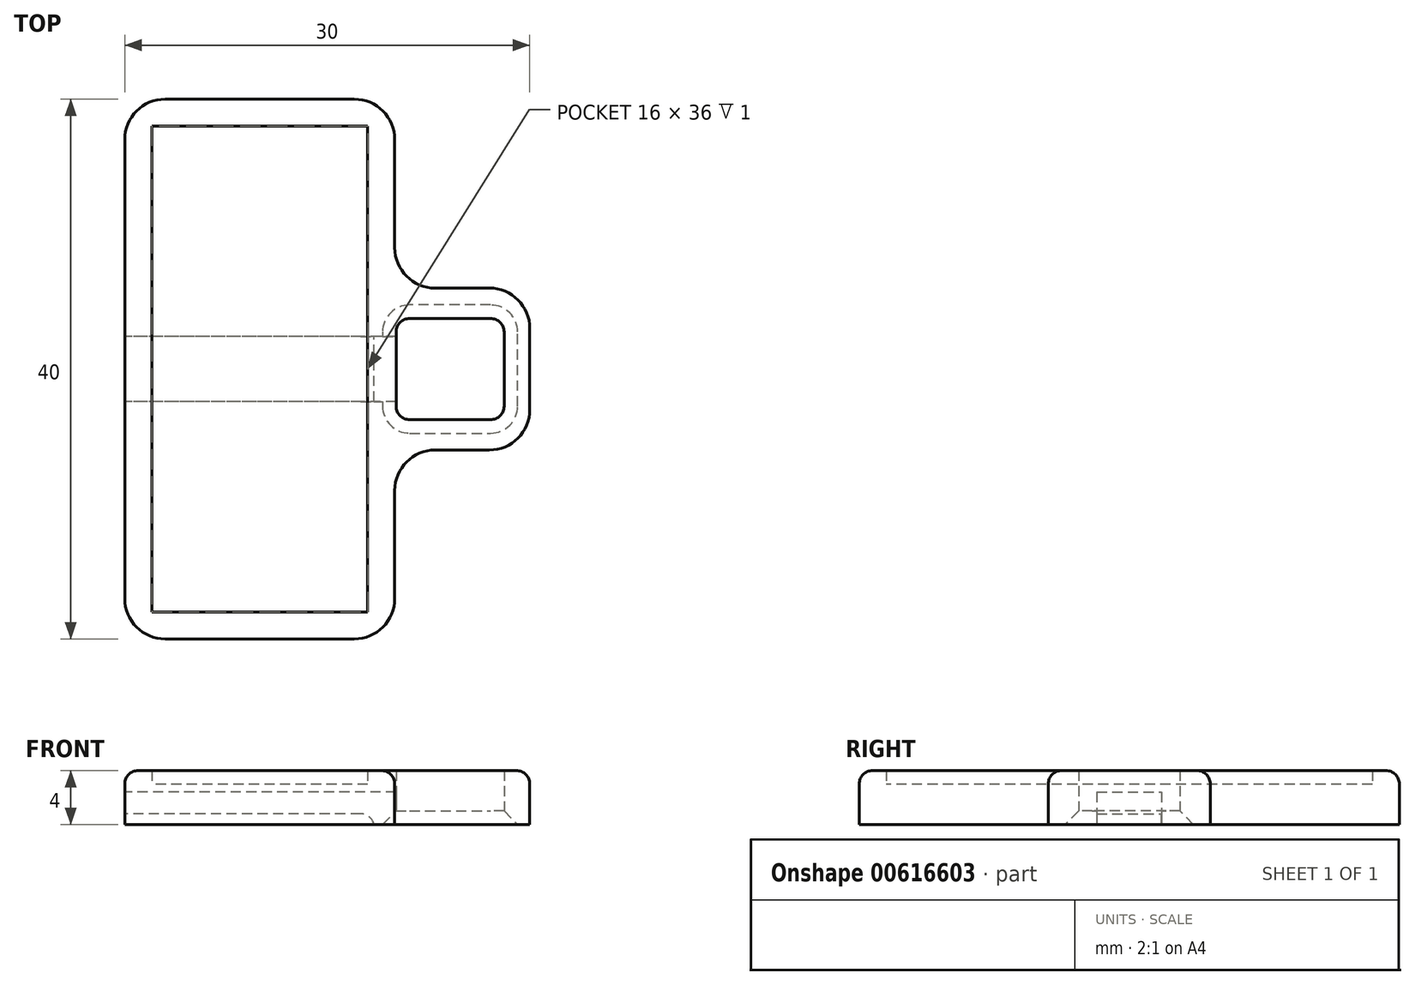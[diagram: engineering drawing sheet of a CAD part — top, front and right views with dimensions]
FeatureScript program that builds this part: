
annotation { "Feature Type Name" : "Feature", "Feature Type Description" : "" }
export const myFeature = defineFeature(function(context is Context, id is Id, definition is map)
    precondition{}
    {
        {
            var Q0;
            Q0=qCreatedBy(makeId("Top.planeOp"),FACE);
            var sketch = newSketch(context, id + "F0", { "sketchPlane" : qUnion([Q0])});
            skLineSegment(sketch, "E0.bottom", {"start": v(7, 20) * mm, "end": v(-7, 20) * mm});
            skLineSegment(sketch, "E0.top", {"start": v(7, -20) * mm, "end": v(-7, -20) * mm});
            skLineSegment(sketch, "E0.left", {"start": v(10, -9) * mm, "end": v(10, -17) * mm});
            skLineSegment(sketch, "E0.right", {"start": v(-10, 17) * mm, "end": v(-10, -17) * mm});
            skPoint(sketch, "E0.middle", {"position": v(0, 0) * mm});
            skLineSegment(sketch, "E1.bottom", {"start": v(13, 6) * mm, "end": v(17, 6) * mm});
            skLineSegment(sketch, "E1.top", {"start": v(13, -6) * mm, "end": v(17, -6) * mm});
            skLineSegment(sketch, "E1.right", {"start": v(20, 3) * mm, "end": v(20, -3) * mm});
            skPoint(sketch, "E1.middle", {"position": v(14.1, 0) * mm});
            skLineSegment(sketch, "E2.0", {"start": v(8, 18) * mm, "end": v(-8, 18) * mm});
            skLineSegment(sketch, "E2.1", {"start": v(8, 18) * mm, "end": v(8, -18) * mm});
            skLineSegment(sketch, "E2.2", {"start": v(8, -18) * mm, "end": v(-8, -18) * mm});
            skLineSegment(sketch, "E2.3", {"start": v(-8, 18) * mm, "end": v(-8, -18) * mm});
            skPoint(sketch, "E3.visualSharp", {"position": v(-10, 20) * mm});
            skArc(sketch, "E3.filletArc", {"start": v(-7, 20) * mm, "mid": v(-9.12, 19.12) * mm, "end": v(-10, 17) * mm});
            skPoint(sketch, "E4.visualSharp", {"position": v(10, 20) * mm});
            skArc(sketch, "E4.filletArc", {"start": v(10, 17) * mm, "mid": v(9.12, 19.12) * mm, "end": v(7, 20) * mm});
            skPoint(sketch, "E5.visualSharp", {"position": v(10, -20) * mm});
            skArc(sketch, "E5.filletArc", {"start": v(7, -20) * mm, "mid": v(9.12, -19.12) * mm, "end": v(10, -17) * mm});
            skPoint(sketch, "E6.visualSharp", {"position": v(-10, -20) * mm});
            skArc(sketch, "E6.filletArc", {"start": v(-10, -17) * mm, "mid": v(-9.12, -19.12) * mm, "end": v(-7, -20) * mm});
            skPoint(sketch, "E7.visualSharp", {"position": v(20, 6) * mm});
            skArc(sketch, "E7.filletArc", {"start": v(20, 3) * mm, "mid": v(19.12, 5.12) * mm, "end": v(17, 6) * mm});
            skPoint(sketch, "E8.visualSharp", {"position": v(20, -6) * mm});
            skArc(sketch, "E8.filletArc", {"start": v(17, -6) * mm, "mid": v(19.12, -5.12) * mm, "end": v(20, -3) * mm});
            skPoint(sketch, "E9.newPointA", {"position": v(12, -6) * mm});
            skArc(sketch, "E9.filletArc", {"start": v(13, -6) * mm, "mid": v(10.88, -6.88) * mm, "end": v(10, -9) * mm});
            skLineSegment(sketch, "E10", {"start": v(10, 17) * mm, "end": v(10, 9) * mm});
            skPoint(sketch, "E11.visualSharp", {"position": v(10, 6) * mm});
            skArc(sketch, "E11.filletArc", {"start": v(10, 9) * mm, "mid": v(10.88, 6.88) * mm, "end": v(13, 6) * mm});
            skLineSegment(sketch, "E12.bottom", {"start": v(11.1, 3.75) * mm, "end": v(17.1, 3.75) * mm});
            skLineSegment(sketch, "E12.top", {"start": v(11.1, -3.75) * mm, "end": v(17.1, -3.75) * mm});
            skLineSegment(sketch, "E12.left", {"start": v(10.1, 2.75) * mm, "end": v(10.1, -2.75) * mm});
            skLineSegment(sketch, "E12.right", {"start": v(18.1, 2.75) * mm, "end": v(18.1, -2.75) * mm});
            skPoint(sketch, "E13.visualSharp", {"position": v(10.1, 3.75) * mm});
            skArc(sketch, "E13.filletArc", {"start": v(11.1, 3.75) * mm, "mid": v(10.4, 3.46) * mm, "end": v(10.1, 2.75) * mm});
            skPoint(sketch, "E14.visualSharp", {"position": v(10.1, -3.75) * mm});
            skArc(sketch, "E14.filletArc", {"start": v(10.1, -2.75) * mm, "mid": v(10.4, -3.46) * mm, "end": v(11.1, -3.75) * mm});
            skPoint(sketch, "E15.visualSharp", {"position": v(18.1, -3.75) * mm});
            skArc(sketch, "E15.filletArc", {"start": v(17.1, -3.75) * mm, "mid": v(17.8, -3.46) * mm, "end": v(18.1, -2.75) * mm});
            skPoint(sketch, "E16.visualSharp", {"position": v(18.1, 3.75) * mm});
            skArc(sketch, "E16.filletArc", {"start": v(18.1, 2.75) * mm, "mid": v(17.8, 3.46) * mm, "end": v(17.1, 3.75) * mm});
            skSolve(sketch);
        }
        {
            var Q0;
            Q0=makeQuery(id+"F0.imprint","IMPRINT",FACE,{"disambiguationData":[TD([[makeQuery(id+"F0.imprint","IMPRINT",EDGE,{"derivedFrom":sQuery(id+"F0.wireOp",EDGE,"E0.bottom")}),1.0]])]});
            extrude(context, id + "F1", {"entities" : qUnion([Q0]), "depth" : 4 * mm, "offsetDistance" : 25 * mm});
        }
        {
            var Q0;
            Q0=makeQuery(id+"F0.imprint","IMPRINT",FACE,{"disambiguationData":[TD([[makeQuery(id+"F0.imprint","IMPRINT",EDGE,{"derivedFrom":sQuery(id+"F0.wireOp",EDGE,"E2.0")}),1.0]])]});
            extrude(context, id + "F2", {"entities" : qUnion([Q0]), "operationType" : NewBodyOperationType.ADD, "depth" : 3 * mm, "offsetDistance" : 25 * mm});
        }
        {
            var Q0;
            Q0=makeQuery(id+"F1.opExtrude","SWEPT_FACE",FACE,{"disambiguationData":[OSD([sQuery(id+"F0.wireOp",EDGE,"E0.right")])]});
            var sketch = newSketch(context, id + "F3", { "sketchPlane" : qUnion([Q0])});
            skLineSegment(sketch, "E17.bottom", {"start": v(2.4, 2.4) * mm, "end": v(-2.4, 2.4) * mm});
            skLineSegment(sketch, "E17.top", {"start": v(2.4, 0.8) * mm, "end": v(-2.4, 0.8) * mm});
            skLineSegment(sketch, "E17.left", {"start": v(2.4, 2.4) * mm, "end": v(2.4, 0.8) * mm});
            skLineSegment(sketch, "E17.right", {"start": v(-2.4, 2.4) * mm, "end": v(-2.4, 0.8) * mm});
            skPoint(sketch, "E17.middle", {"position": v(0, 1.6) * mm});
            skSolve(sketch);
        }
        {
            var Q0;
            Q0=makeQuery(id+"F3.imprint","IMPRINT",FACE,{"disambiguationData":[TD([[makeQuery(id+"F3.imprint","IMPRINT",EDGE,{"derivedFrom":sQuery(id+"F3.wireOp",EDGE,"E17.bottom")}),1.0]])]});
            var Q1;
            Q1=makeQuery(id+"F1.opExtrude","SWEPT_FACE",FACE,{"disambiguationData":[OSD([sQuery(id+"F0.wireOp",EDGE,"E12.left")])]});
            extrude(context, id + "F4", {"entities" : qUnion([Q0]), "operationType" : NewBodyOperationType.REMOVE, "endBound" : BoundingType.UP_TO_SURFACE, "oppositeDirection" : true, "depth" : 25 * mm, "endBoundEntityFace" : qUnion([Q1]), "offsetDistance" : 25 * mm});
        }
        {
            var Q0;
            Q0=makeQuery(id+"F1.opExtrude","CAP_EDGE",EDGE,{"disambiguationData":[OSD([sQuery(id+"F0.wireOp",EDGE,"E12.right")])],"isStart":true});
            chamfer(context, id + "F5", {"entities" : qUnion([Q0]), "width" : 1 * mm, "tangentPropagation" : true});
        }
        {
            var Q0;
            Q0=makeQuery(id+"F5.opChamfer","BLEND_EDGE",EDGE,{"blendedFrom":[makeQuery(id+"F1.opExtrude","CAP_EDGE",EDGE,{"disambiguationData":[OSD([sQuery(id+"F0.wireOp",EDGE,"E12.left")])],"isStart":true}),makeQuery(id+"F4.boolean.opBoolean","COPY",FACE,{"derivedFrom":makeQuery(id+"F4.opExtrude","SWEPT_FACE",FACE,{"disambiguationData":[OSD([sQuery(id+"F3.wireOp",EDGE,"E17.top")])]})})],"blendedInto":[makeQuery(id+"F4.boolean.opBoolean","COPY",FACE,{"derivedFrom":makeQuery(id+"F4.opExtrude","SWEPT_FACE",FACE,{"disambiguationData":[OSD([sQuery(id+"F3.wireOp",EDGE,"E17.top")])]})})]});
            fillet(context, id + "F6", {"entities" : qUnion([Q0]), "radius" : 1 * mm, "tangentPropagation" : true, "allowEdgeOverflow" : false});
        }
        {
            var Q0;
            Q0=makeQuery(id+"F1.opExtrude","CAP_EDGE",EDGE,{"disambiguationData":[OSD([sQuery(id+"F0.wireOp",EDGE,"E0.right")])],"isStart":false});
            fillet(context, id + "F7", {"entities" : qUnion([Q0]), "radius" : 1 * mm, "tangentPropagation" : true, "allowEdgeOverflow" : false});
        }
    });
